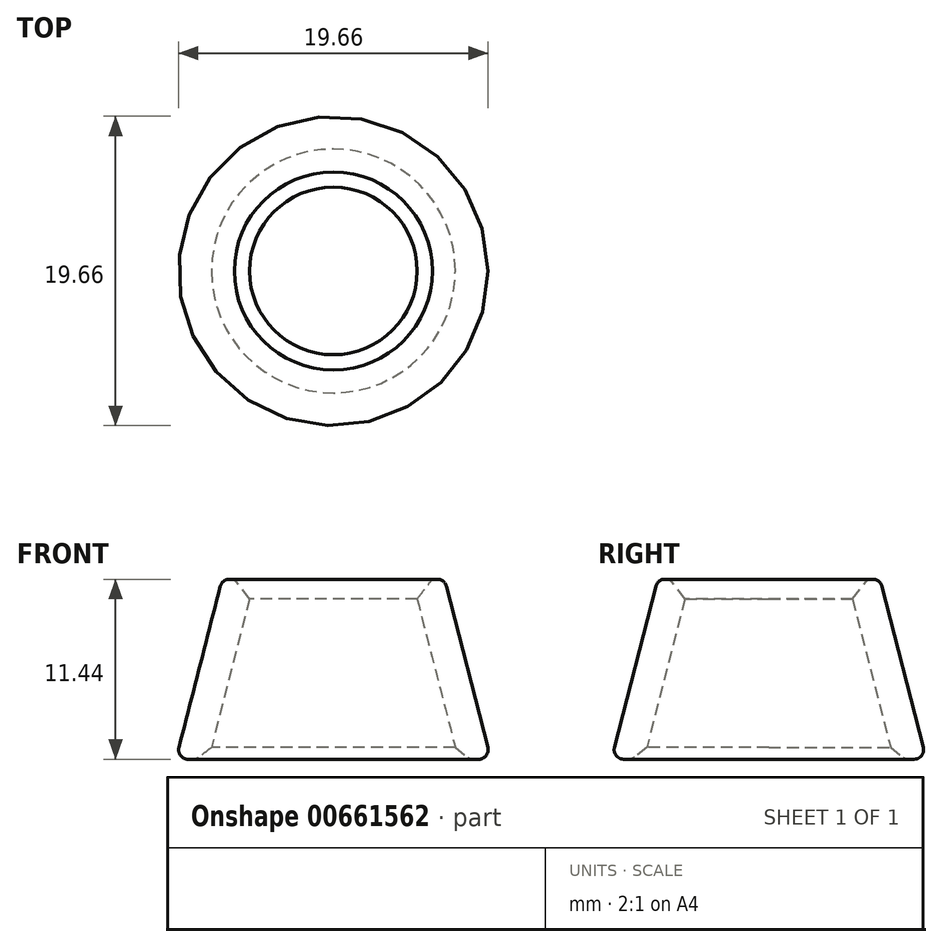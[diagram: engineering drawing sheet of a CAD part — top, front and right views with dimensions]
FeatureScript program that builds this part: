
annotation { "Feature Type Name" : "Feature", "Feature Type Description" : "" }
export const myFeature = defineFeature(function(context is Context, id is Id, definition is map)
    precondition{}
    {
        {
            var Q0;
            Q0=qCreatedBy(makeId("Front.planeOp"),FACE);
            var sketch = newSketch(context, id + "F0", { "sketchPlane" : qUnion([Q0])});
            skLineSegment(sketch, "E0", {"start": v(-7.94, 0.56) * mm, "end": v(-5, 12) * mm});
            skLineSegment(sketch, "E1.0", {"start": v(-10, 0.56) * mm, "end": v(-7.06, 12) * mm});
            skLineSegment(sketch, "E2", {"start": v(-10, 0.56) * mm, "end": v(-7.94, 0.56) * mm});
            skPoint(sketch, "E3.orphan", {"position": v(-8.08, 0) * mm});
            skLineSegment(sketch, "E4", {"start": v(-5, 12) * mm, "end": v(-7.06, 12) * mm});
            skLineSegment(sketch, "E5", {"start": v(0, 0) * mm, "end": v(0, 38.9) * mm, "construction": true});
            skSolve(sketch);
        }
        {
            var Q0;
            Q0=makeQuery(id+"F0.imprint","IMPRINT",FACE,{"disambiguationData":[TD([[makeQuery(id+"F0.imprint","IMPRINT",EDGE,{"derivedFrom":sQuery(id+"F0.wireOp",EDGE,"E0")}),1.0]])]});
            var Q1;
            Q1=sQuery(id+"F0.wireOp",EDGE,"E5");
            revolve(context, id + "F1", {"entities" : qUnion([Q0]), "axis" : qUnion([Q1]), "revolveType" : RevolveType.FULL});
        }
        {
            var Q0;
            Q0=makeQuery(id+"F1.opRevolve","SWEPT_EDGE",EDGE,{"disambiguationData":[OSD([sQuery(id+"F0.wireOp",EDGE,"E0"),sQuery(id+"F0.wireOp",EDGE,"E4")])]});
            var Q1;
            Q1=makeQuery(id+"F1.opRevolve","SWEPT_EDGE",EDGE,{"disambiguationData":[OSD([sQuery(id+"F0.wireOp",EDGE,"E0"),sQuery(id+"F0.wireOp",EDGE,"E2")])]});
            chamfer(context, id + "F2", {"entities" : qUnion([Q0, Q1]), "width" : 1 * mm, "tangentPropagation" : true});
        }
        {
            var Q0;
            Q0=makeQuery(id+"F1.opRevolve","SWEPT_EDGE",EDGE,{"disambiguationData":[OSD([sQuery(id+"F0.wireOp",EDGE,"E1.0"),sQuery(id+"F0.wireOp",EDGE,"E4")])]});
            var Q1;
            Q1=makeQuery(id+"F1.opRevolve","SWEPT_FACE",FACE,{"disambiguationData":[OSD([sQuery(id+"F0.wireOp",EDGE,"E2")])]});
            fillet(context, id + "F3", {"entities" : qUnion([Q0, Q1]), "radius" : .6 * mm, "tangentPropagation" : true, "allowEdgeOverflow" : false});
        }
    });
